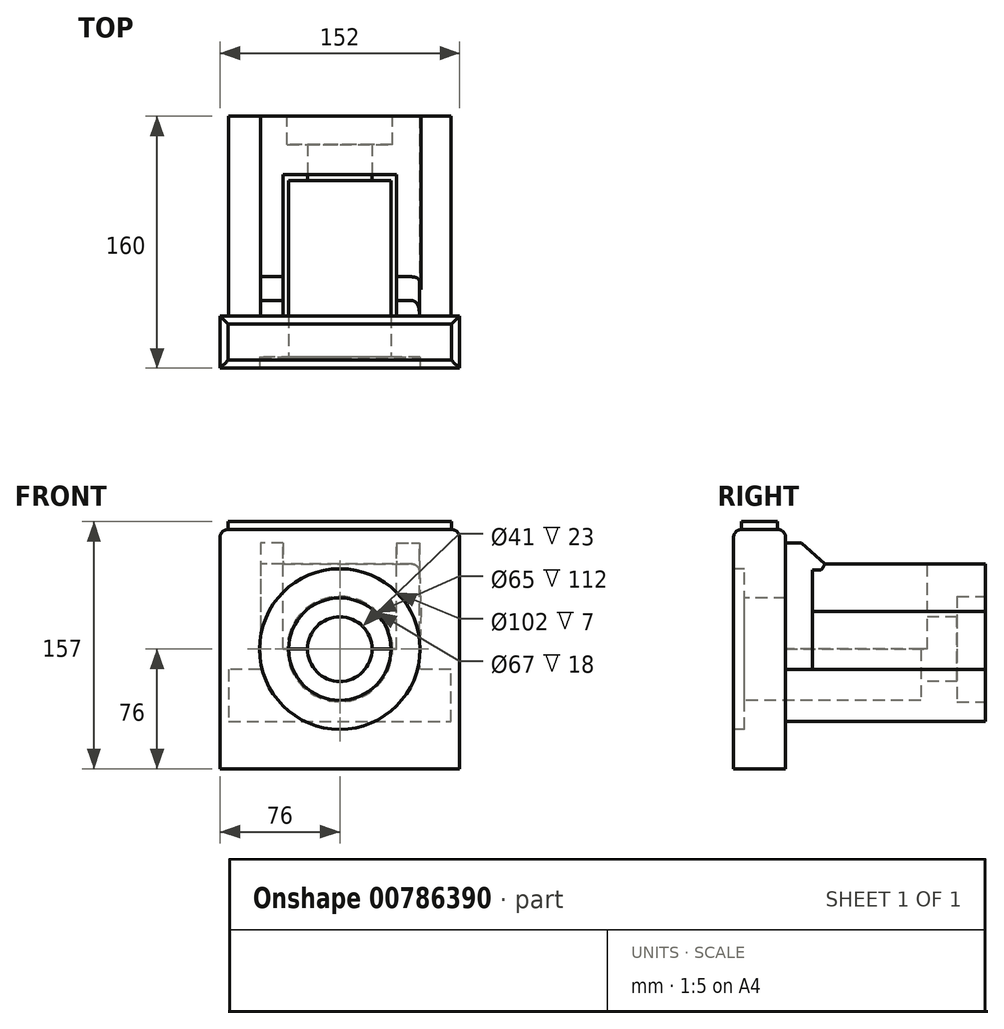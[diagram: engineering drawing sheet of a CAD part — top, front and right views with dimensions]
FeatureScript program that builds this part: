
annotation { "Feature Type Name" : "Feature", "Feature Type Description" : "" }
export const myFeature = defineFeature(function(context is Context, id is Id, definition is map)
    precondition{}
    {
        {
            var Q0;
            Q0=qCreatedBy(makeId("Front.planeOp"),FACE);
            var sketch = newSketch(context, id + "F0", { "sketchPlane" : qUnion([Q0])});
            skLineSegment(sketch, "E0.bottom", {"start": v(76, 76) * mm, "end": v(-76, 76) * mm});
            skLineSegment(sketch, "E0.top", {"start": v(76, -76) * mm, "end": v(-76, -76) * mm});
            skLineSegment(sketch, "E0.left", {"start": v(76, 76) * mm, "end": v(76, -76) * mm});
            skLineSegment(sketch, "E0.right", {"start": v(-76, 76) * mm, "end": v(-76, -76) * mm});
            skPoint(sketch, "E0.middle", {"position": v(0, 0) * mm});
            skSolve(sketch);
        }
        {
            var Q0;
            Q0 = qSketchRegion(id + "F0", true);
            extrude(context, id + "F1", {"entities" : qUnion([Q0]), "oppositeDirection" : true, "depth" : 33 * mm, "offsetDistance" : 25 * mm});
        }
        {
            var Q0;
            Q0=makeQuery(id+"F1.opExtrude","CAP_FACE",FACE,{"disambiguationData":[OSD([sQuery(id+"F0.wireOp",EDGE,"E0.bottom"),sQuery(id+"F0.wireOp",EDGE,"E0.top"),sQuery(id+"F0.wireOp",EDGE,"E0.left"),sQuery(id+"F0.wireOp",EDGE,"E0.right")])],"isStart":false});
            var sketch = newSketch(context, id + "F2", { "sketchPlane" : qUnion([Q0])});
            skLineSegment(sketch, "E1", {"start": v(-50.5, 54) * mm, "end": v(50.5, 54) * mm});
            skLineSegment(sketch, "E2", {"start": v(50.5, 54) * mm, "end": v(50.5, -13) * mm});
            skLineSegment(sketch, "E3", {"start": v(50.5, -13) * mm, "end": v(70.5, -13) * mm});
            skLineSegment(sketch, "E4", {"start": v(70.5, -13) * mm, "end": v(70.5, -46) * mm});
            skLineSegment(sketch, "E5", {"start": v(70.5, -46) * mm, "end": v(-70.5, -46) * mm});
            skLineSegment(sketch, "E6", {"start": v(-70.5, -46) * mm, "end": v(-70.5, -13) * mm});
            skLineSegment(sketch, "E7", {"start": v(-70.5, -13) * mm, "end": v(-50.5, -13) * mm});
            skLineSegment(sketch, "E8", {"start": v(-50.5, -13) * mm, "end": v(-50.5, 54) * mm});
            skSolve(sketch);
        }
        {
            var Q0;
            Q0 = qSketchRegion(id + "F2", true);
            extrude(context, id + "F3", {"entities" : qUnion([Q0]), "operationType" : NewBodyOperationType.ADD, "depth" : 127 * mm, "offsetDistance" : 25 * mm});
        }
        {
            var Q0;
            Q0=qCreatedBy(makeId("Front.planeOp"),FACE);
            var sketch = newSketch(context, id + "F4", { "sketchPlane" : qUnion([Q0])});
            skCircle(sketch, "E9", {"center": v(0, 0) * mm, "radius": 20.5 * mm});
            skCircle(sketch, "E10", {"center": v(0, 0) * mm, "radius": 32.5 * mm});
            skCircle(sketch, "E11", {"center": v(0, 0) * mm, "radius": 51 * mm});
            skSolve(sketch);
        }
        {
            var Q0;
            Q0=makeQuery(id+"F4.imprint","IMPRINT",FACE,{"disambiguationData":[TD([[makeQuery(id+"F4.imprint","IMPRINT",EDGE,{"derivedFrom":sQuery(id+"F4.wireOp",EDGE,"E9")}),1.0]])]});
            extrude(context, id + "F5", {"entities" : qUnion([Q0]), "operationType" : NewBodyOperationType.REMOVE, "oppositeDirection" : true, "depth" : 156 * mm, "offsetDistance" : 25 * mm});
        }
        {
            var Q0;
            Q0=makeQuery(id+"F4.imprint","IMPRINT",FACE,{"disambiguationData":[TD([[makeQuery(id+"F4.imprint","IMPRINT",EDGE,{"derivedFrom":sQuery(id+"F4.wireOp",EDGE,"E9")}),-1.0]])]});
            var Q1;
            Q1=makeQuery(id+"F4.imprint","IMPRINT",FACE,{"disambiguationData":[TD([[makeQuery(id+"F4.imprint","IMPRINT",EDGE,{"derivedFrom":sQuery(id+"F4.wireOp",EDGE,"E9")}),1.0]])]});
            extrude(context, id + "F6", {"entities" : qUnion([Q0, Q1]), "operationType" : NewBodyOperationType.REMOVE, "oppositeDirection" : true, "depth" : 119 * mm, "offsetDistance" : 25 * mm});
        }
        {
            var Q0;
            Q0 = qSketchRegion(id + "F4", true);
            var Q1;
            Q1=makeQuery(id+"F4.imprint","IMPRINT",FACE,{"disambiguationData":[TD([[makeQuery(id+"F4.imprint","IMPRINT",EDGE,{"derivedFrom":sQuery(id+"F4.wireOp",EDGE,"E10")}),-1.0]])]});
            extrude(context, id + "F7", {"entities" : qUnion([Q0, Q1]), "operationType" : NewBodyOperationType.REMOVE, "oppositeDirection" : true, "depth" : 7 * mm, "offsetDistance" : 25 * mm});
        }
        {
            var Q0;
            Q0=makeQuery(id+"F3.opExtrude","CAP_FACE",FACE,{"disambiguationData":[OSD([sQuery(id+"F2.wireOp",EDGE,"E1"),sQuery(id+"F2.wireOp",EDGE,"E2"),sQuery(id+"F2.wireOp",EDGE,"E3"),sQuery(id+"F2.wireOp",EDGE,"E4"),sQuery(id+"F2.wireOp",EDGE,"E5"),sQuery(id+"F2.wireOp",EDGE,"E6"),sQuery(id+"F2.wireOp",EDGE,"E7"),sQuery(id+"F2.wireOp",EDGE,"E8")])],"isStart":false});
            var sketch = newSketch(context, id + "F8", { "sketchPlane" : qUnion([Q0])});
            skCircle(sketch, "E12", {"center": v(0, 0) * mm, "radius": 33.5 * mm});
            skSolve(sketch);
        }
        {
            var Q0;
            Q0 = qSketchRegion(id + "F8", true);
            extrude(context, id + "F9", {"entities" : qUnion([Q0]), "operationType" : NewBodyOperationType.REMOVE, "oppositeDirection" : true, "depth" : 18 * mm, "offsetDistance" : 25 * mm});
        }
        {
            var Q0;
            Q0=makeQuery(id+"F3.opExtrude","SWEPT_FACE",FACE,{"disambiguationData":[OSD([sQuery(id+"F2.wireOp",EDGE,"E1")])]});
            var sketch = newSketch(context, id + "F10", { "sketchPlane" : qUnion([Q0])});
            skLineSegment(sketch, "E13.bottom", {"start": v(-36, 33) * mm, "end": v(36, 33) * mm});
            skLineSegment(sketch, "E13.top", {"start": v(-36, 123) * mm, "end": v(36, 123) * mm});
            skLineSegment(sketch, "E13.left", {"start": v(-36, 33) * mm, "end": v(-36, 123) * mm});
            skLineSegment(sketch, "E13.right", {"start": v(36, 33) * mm, "end": v(36, 123) * mm});
            skSolve(sketch);
        }
        {
            var Q0;
            Q0 = qSketchRegion(id + "F10", true);
            extrude(context, id + "F11", {"entities" : qUnion([Q0]), "operationType" : NewBodyOperationType.REMOVE, "oppositeDirection" : true, "depth" : 54 * mm, "offsetDistance" : 25 * mm});
        }
        {
            var Q0;
            Q0=makeQuery(id+"F3.opExtrude","SWEPT_FACE",FACE,{"disambiguationData":[OSD([sQuery(id+"F2.wireOp",EDGE,"E8")])]});
            var sketch = newSketch(context, id + "F12", { "sketchPlane" : qUnion([Q0])});
            skLineSegment(sketch, "E14", {"start": v(33, 54) * mm, "end": v(33, 67.5) * mm});
            skLineSegment(sketch, "E15", {"start": v(33, 67.5) * mm, "end": v(43, 67.5) * mm});
            skLineSegment(sketch, "E16", {"start": v(43, 67.5) * mm, "end": v(58, 54) * mm});
            skLineSegment(sketch, "E17", {"start": v(58, 54) * mm, "end": v(33, 54) * mm});
            skSolve(sketch);
        }
        {
            var Q0;
            Q0 = qSketchRegion(id + "F12", true);
            extrude(context, id + "F13", {"entities" : qUnion([Q0]), "operationType" : NewBodyOperationType.ADD, "oppositeDirection" : true, "depth" : 14.5 * mm, "offsetDistance" : 25 * mm});
        }
        {
            var Q0;
            Q0=makeQuery(id+"F3.opExtrude","SWEPT_FACE",FACE,{"disambiguationData":[OSD([sQuery(id+"F2.wireOp",EDGE,"E2")])]});
            var sketch = newSketch(context, id + "F14", { "sketchPlane" : qUnion([Q0])});
            skLineSegment(sketch, "E18", {"start": v(-33, 54) * mm, "end": v(-33, 67.5) * mm});
            skLineSegment(sketch, "E19", {"start": v(-33, 67.5) * mm, "end": v(-43, 67.5) * mm});
            skLineSegment(sketch, "E20", {"start": v(-43, 67.5) * mm, "end": v(-58, 54) * mm});
            skLineSegment(sketch, "E21", {"start": v(-58, 54) * mm, "end": v(-33, 54) * mm});
            skSolve(sketch);
        }
        {
            var Q0;
            Q0 = qSketchRegion(id + "F14", true);
            extrude(context, id + "F15", {"entities" : qUnion([Q0]), "operationType" : NewBodyOperationType.ADD, "oppositeDirection" : true, "depth" : 14.5 * mm, "offsetDistance" : 25 * mm});
        }
        {
            var Q0;
            Q0=makeQuery(id+"F1.opExtrude","CAP_EDGE",EDGE,{"disambiguationData":[OSD([sQuery(id+"F0.wireOp",EDGE,"E0.bottom")])],"isStart":false});
            var Q1;
            Q1=makeQuery(id+"F1.opExtrude","SWEPT_EDGE",EDGE,{"disambiguationData":[OSD([sQuery(id+"F0.wireOp",EDGE,"E0.bottom"),sQuery(id+"F0.wireOp",EDGE,"E0.left")])]});
            var Q2;
            Q2=makeQuery(id+"F1.opExtrude","CAP_EDGE",EDGE,{"disambiguationData":[OSD([sQuery(id+"F0.wireOp",EDGE,"E0.bottom")])],"isStart":true});
            var Q3;
            Q3=makeQuery(id+"F1.opExtrude","SWEPT_EDGE",EDGE,{"disambiguationData":[OSD([sQuery(id+"F0.wireOp",EDGE,"E0.bottom"),sQuery(id+"F0.wireOp",EDGE,"E0.right")])]});
            fillet(context, id + "F16", {"entities" : qUnion([Q0, Q1, Q2, Q3]), "radius" : 5 * mm, "tangentPropagation" : true, "allowEdgeOverflow" : false});
        }
        {
            var Q0;
            Q0=makeQuery(id+"F1.opExtrude","SWEPT_FACE",FACE,{"disambiguationData":[OSD([sQuery(id+"F0.wireOp",EDGE,"E0.bottom")])]});
            var sketch = newSketch(context, id + "F17", { "sketchPlane" : qUnion([Q0])});
            skLineSegment(sketch, "E22", {"start": v(-71, 5) * mm, "end": v(-71, 28) * mm});
            skLineSegment(sketch, "E23", {"start": v(-71, 28) * mm, "end": v(71, 28) * mm});
            skLineSegment(sketch, "E24", {"start": v(71, 28) * mm, "end": v(71, 5) * mm});
            skLineSegment(sketch, "E25", {"start": v(71, 5) * mm, "end": v(-71, 5) * mm});
            skSolve(sketch);
        }
        {
            var Q0;
            Q0 = qSketchRegion(id + "F17", true);
            extrude(context, id + "F18", {"entities" : qUnion([Q0]), "operationType" : NewBodyOperationType.ADD, "depth" : 5 * mm, "offsetDistance" : 25 * mm});
        }
        {
            var Q0;
            Q0=makeQuery(id+"F3.opExtrude","CAP_FACE",FACE,{"disambiguationData":[OSD([sQuery(id+"F2.wireOp",EDGE,"E1"),sQuery(id+"F2.wireOp",EDGE,"E2"),sQuery(id+"F2.wireOp",EDGE,"E3"),sQuery(id+"F2.wireOp",EDGE,"E4"),sQuery(id+"F2.wireOp",EDGE,"E5"),sQuery(id+"F2.wireOp",EDGE,"E6"),sQuery(id+"F2.wireOp",EDGE,"E7"),sQuery(id+"F2.wireOp",EDGE,"E8")])],"isStart":false});
            var sketch = newSketch(context, id + "F19", { "sketchPlane" : qUnion([Q0])});
            skLineSegment(sketch, "E26", {"start": v(-50.5, 54) * mm, "end": v(-51.55, 23.9) * mm});
            skLineSegment(sketch, "E27", {"start": v(-51.55, 23.9) * mm, "end": v(-50.5, -13) * mm});
            skLineSegment(sketch, "E28", {"start": v(-50.5, 54) * mm, "end": v(-50.5, -13) * mm});
            skSolve(sketch);
        }
        {
            var Q0;
            Q0 = qSketchRegion(id + "F19", true);
            extrude(context, id + "F20", {"entities" : qUnion([Q0]), "operationType" : NewBodyOperationType.ADD, "oppositeDirection" : true, "depth" : 110 * mm, "offsetDistance" : 25 * mm});
        }
        {
            var Q0;
            {var subQ0=sQuery(id+"F2.wireOp",EDGE,"E1");Q0=makeQuery(id+"F20.boolean.opBoolean","MERGE",EDGE,{"derivedFrom":[makeQuery(id+"F3.opExtrude","SWEPT_EDGE",EDGE,{"disambiguationData":[OSD([subQ0,sQuery(id+"F2.wireOp",EDGE,"E8")])]}),makeQuery(id+"F20.opExtrude","SWEPT_EDGE",EDGE,{"disambiguationData":[OSD([subQ0,sQuery(id+"F19.wireOp",EDGE,"E26"),sQuery(id+"F19.wireOp",EDGE,"E28")])]})]});}
            var Q1;
            Q1=makeQuery(id+"F13.opExtrude","CAP_EDGE",EDGE,{"disambiguationData":[OSD([sQuery(id+"F12.wireOp",EDGE,"E16")])],"isStart":true});
            fillet(context, id + "F21", {"entities" : qUnion([Q0, Q1]), "radius" : 5 * mm, "tangentPropagation" : true, "allowEdgeOverflow" : false});
        }
    });
